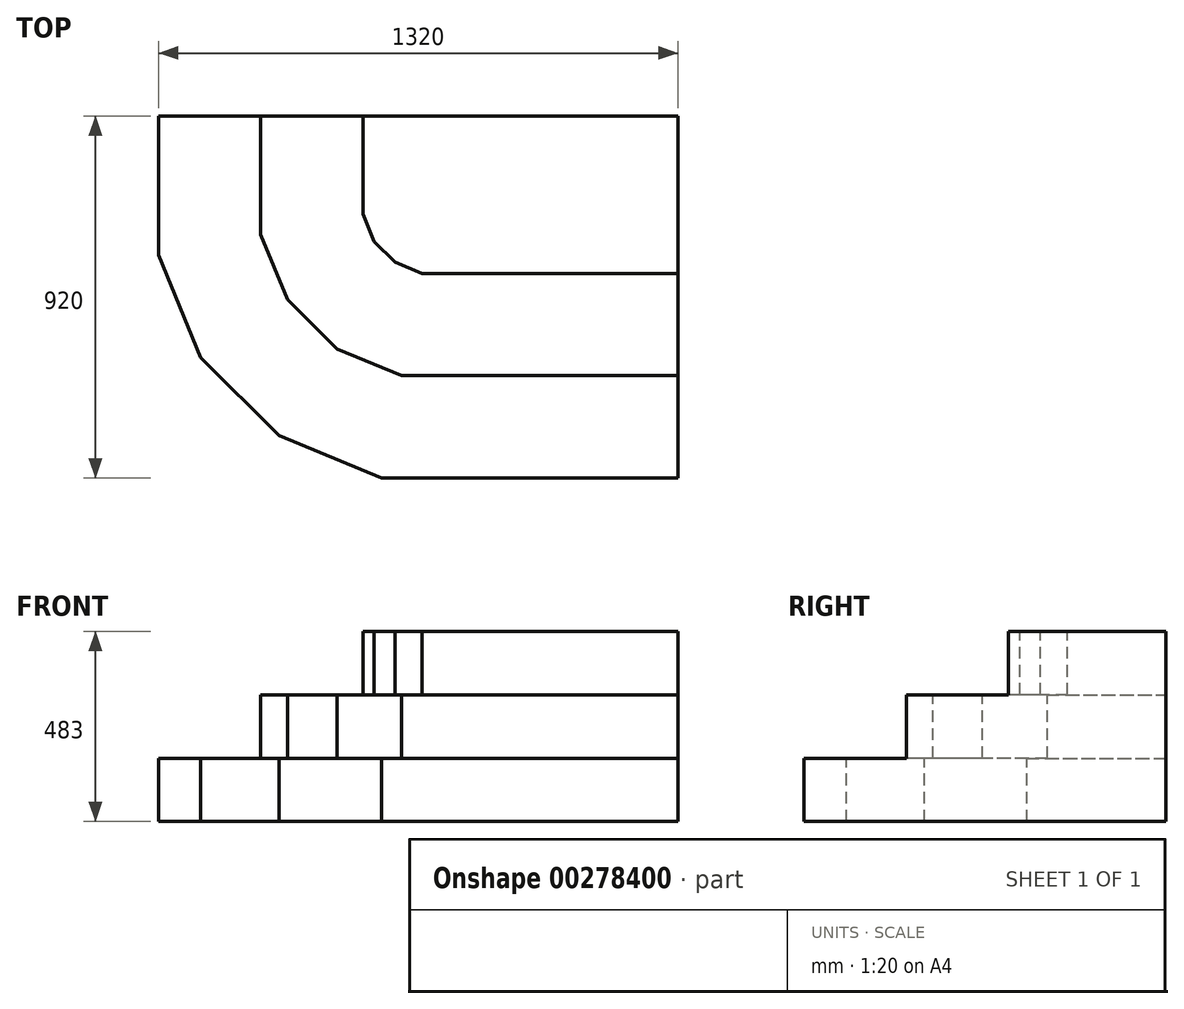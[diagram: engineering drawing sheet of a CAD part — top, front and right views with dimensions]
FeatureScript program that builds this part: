
annotation { "Feature Type Name" : "Feature", "Feature Type Description" : "" }
export const myFeature = defineFeature(function(context is Context, id is Id, definition is map)
    precondition{}
    {
        {
            var Q0;
            Q0=qCreatedBy(makeId("Top.planeOp"),FACE);
            var sketch = newSketch(context, id + "F0", { "sketchPlane" : qUnion([Q0])});
            skLineSegment(sketch, "E0", {"start": v(0, 0) * mm, "end": v(800, 0) * mm});
            skLineSegment(sketch, "E1", {"start": v(800, 0) * mm, "end": v(800, -400) * mm});
            skLineSegment(sketch, "E2", {"start": v(800, -400) * mm, "end": v(150, -400) * mm});
            skLineSegment(sketch, "E3", {"start": v(0, -250) * mm, "end": v(0, 0) * mm});
            skLineSegment(sketch, "E4", {"start": v(0, -250) * mm, "end": v(28.5, -318.82) * mm});
            skLineSegment(sketch, "E5", {"start": v(81.18, -371.5) * mm, "end": v(150, -400) * mm});
            skLineSegment(sketch, "E6", {"start": v(28.5, -318.82) * mm, "end": v(81.18, -371.5) * mm});
            skPoint(sketch, "E7.orphan", {"position": v(43.93, -356.07) * mm});
            skSolve(sketch);
        }
        {
            var Q0;
            Q0=qSketchRegion(id+"F0",true);
            extrude(context, id + "F1", {"entities" : qUnion([Q0]), "oppositeDirection" : true, "depth" : 161 * mm});
        }
        {
            var Q0;
            Q0=makeQuery(id+"F1.opExtrude","CAP_FACE",FACE,{"disambiguationData":[OSD([sQuery(id+"F0.wireOp",EDGE,"E0"),sQuery(id+"F0.wireOp",EDGE,"E1"),sQuery(id+"F0.wireOp",EDGE,"E2"),sQuery(id+"F0.wireOp",EDGE,"E3"),sQuery(id+"F0.wireOp",EDGE,"98b5bb9a-0c86-4538-a68b-eb69053a3bf8")])],"isStart":false});
            var sketch = newSketch(context, id + "F2", { "sketchPlane" : qUnion([Q0])});
            skLineSegment(sketch, "E8.0", {"start": v(-260, 301.72) * mm, "end": v(-260, 0) * mm});
            skLineSegment(sketch, "E8.2", {"start": v(-66.1, 591.91) * mm, "end": v(98.28, 660) * mm});
            skLineSegment(sketch, "E8.3", {"start": v(-191.91, 466.1) * mm, "end": v(-66.1, 591.91) * mm});
            skLineSegment(sketch, "E8.4", {"start": v(-260, 301.72) * mm, "end": v(-191.91, 466.1) * mm});
            skLineSegment(sketch, "E9", {"start": v(-260, 0) * mm, "end": v(800, 0) * mm});
            skLineSegment(sketch, "E10", {"start": v(800, 0) * mm, "end": v(800, 660) * mm});
            skLineSegment(sketch, "E11", {"start": v(98.28, 660) * mm, "end": v(800, 660) * mm});
            skSolve(sketch);
        }
        {
            var Q0;
            Q0=qSketchRegion(id+"F2",true);
            extrude(context, id + "F3", {"entities" : qUnion([Q0]), "operationType" : NewBodyOperationType.ADD, "depth" : 161 * mm});
        }
        {
            var Q0;
            Q0=makeQuery(id+"F3.opExtrude","CAP_FACE",FACE,{"disambiguationData":[OSD([sQuery(id+"F2.wireOp",EDGE,"E8.0"),sQuery(id+"F2.wireOp",EDGE,"E8.2"),sQuery(id+"F2.wireOp",EDGE,"E8.3"),sQuery(id+"F2.wireOp",EDGE,"E8.4"),sQuery(id+"F2.wireOp",EDGE,"E9"),sQuery(id+"F2.wireOp",EDGE,"E10"),sQuery(id+"F2.wireOp",EDGE,"E11")])],"isStart":false});
            var sketch = newSketch(context, id + "F4", { "sketchPlane" : qUnion([Q0])});
            skLineSegment(sketch, "E12.0", {"start": v(-520, 353.43) * mm, "end": v(-520, 0) * mm});
            skLineSegment(sketch, "E12.1", {"start": v(46.57, 920) * mm, "end": v(800, 920) * mm});
            skLineSegment(sketch, "E12.2", {"start": v(-213.38, 812.33) * mm, "end": v(46.57, 920) * mm});
            skLineSegment(sketch, "E12.3", {"start": v(-412.33, 613.38) * mm, "end": v(-213.38, 812.33) * mm});
            skLineSegment(sketch, "E12.4", {"start": v(-520, 353.43) * mm, "end": v(-412.33, 613.38) * mm});
            skLineSegment(sketch, "E13", {"start": v(-520, 0) * mm, "end": v(800, 0) * mm});
            skLineSegment(sketch, "E14", {"start": v(800, 0) * mm, "end": v(800, 920) * mm});
            skSolve(sketch);
        }
        {
            var Q0;
            Q0 = qSketchRegion(id + "F4", true);
            extrude(context, id + "F5", {"entities" : qUnion([Q0]), "operationType" : NewBodyOperationType.ADD, "depth" : 161 * mm});
        }
    });
